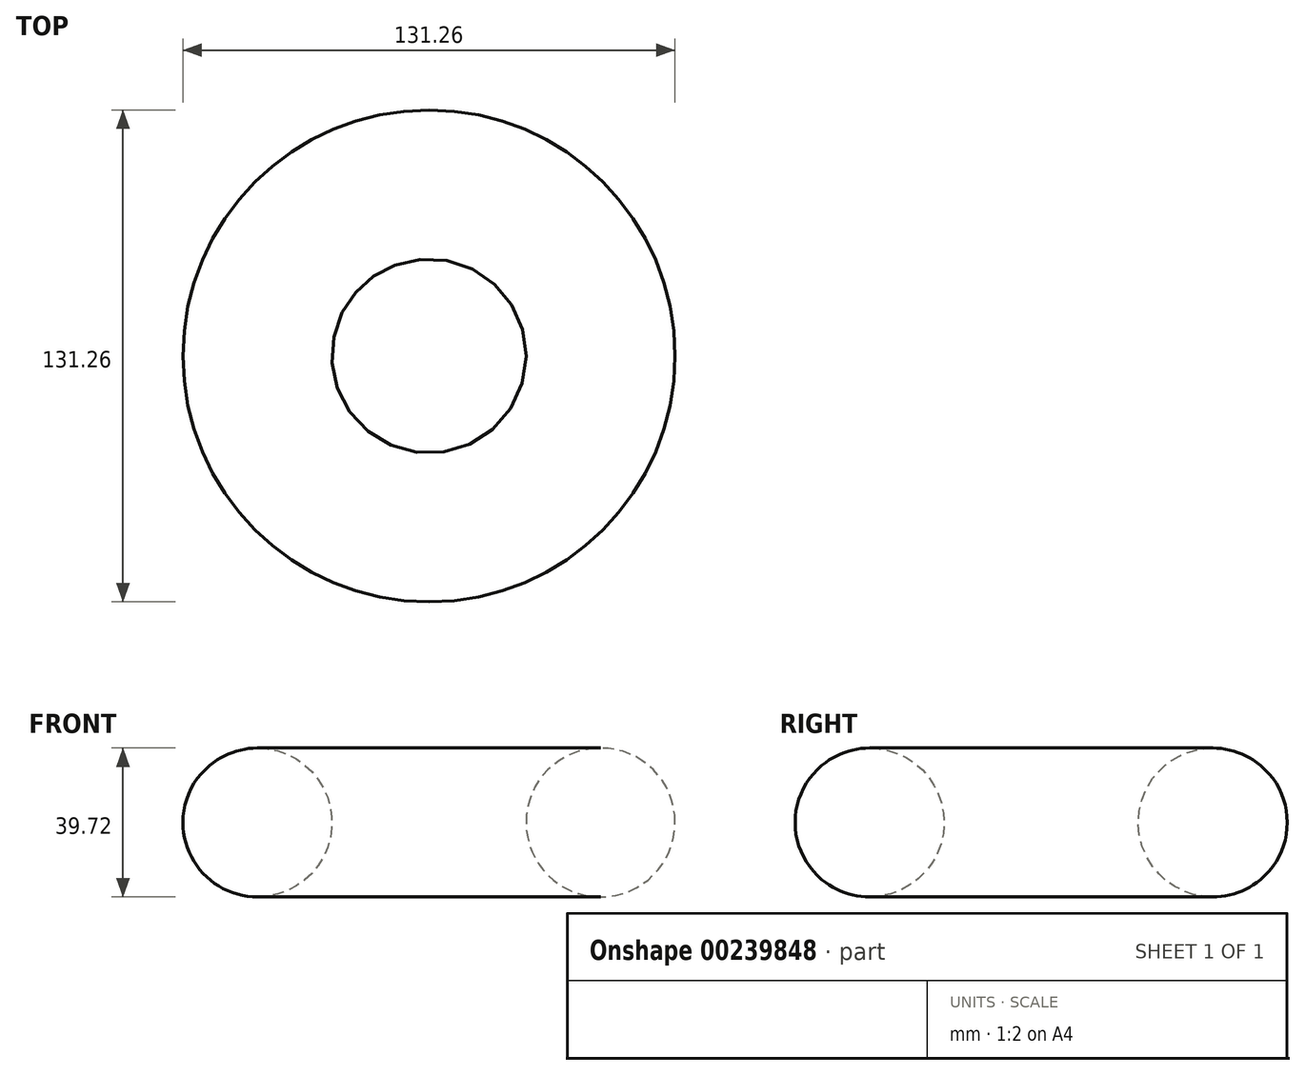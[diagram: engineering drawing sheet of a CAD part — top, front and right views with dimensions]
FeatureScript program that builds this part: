
annotation { "Feature Type Name" : "Feature", "Feature Type Description" : "" }
export const myFeature = defineFeature(function(context is Context, id is Id, definition is map)
    precondition{}
    {
        {
            var Q0;
            Q0=qCreatedBy(makeId("Front.planeOp"),FACE);
            var sketch = newSketch(context, id + "F0", { "sketchPlane" : qUnion([Q0])});
            skCircle(sketch, "E0", {"center": v(-45.76, 0) * mm, "radius": 19.86 * mm});
            skLineSegment(sketch, "E1", {"start": v(0, 73.6) * mm, "end": v(0, -53.2) * mm, "construction": true});
            skSolve(sketch);
        }
        {
            var Q0;
            Q0 = qSketchRegion(id + "F0", true);
            var Q1;
            Q1=sQuery(id+"F0.wireOp",EDGE,"E1");
            revolve(context, id + "F1", {"entities" : qUnion([Q0]), "axis" : qUnion([Q1]), "revolveType" : RevolveType.FULL});
        }
    });
